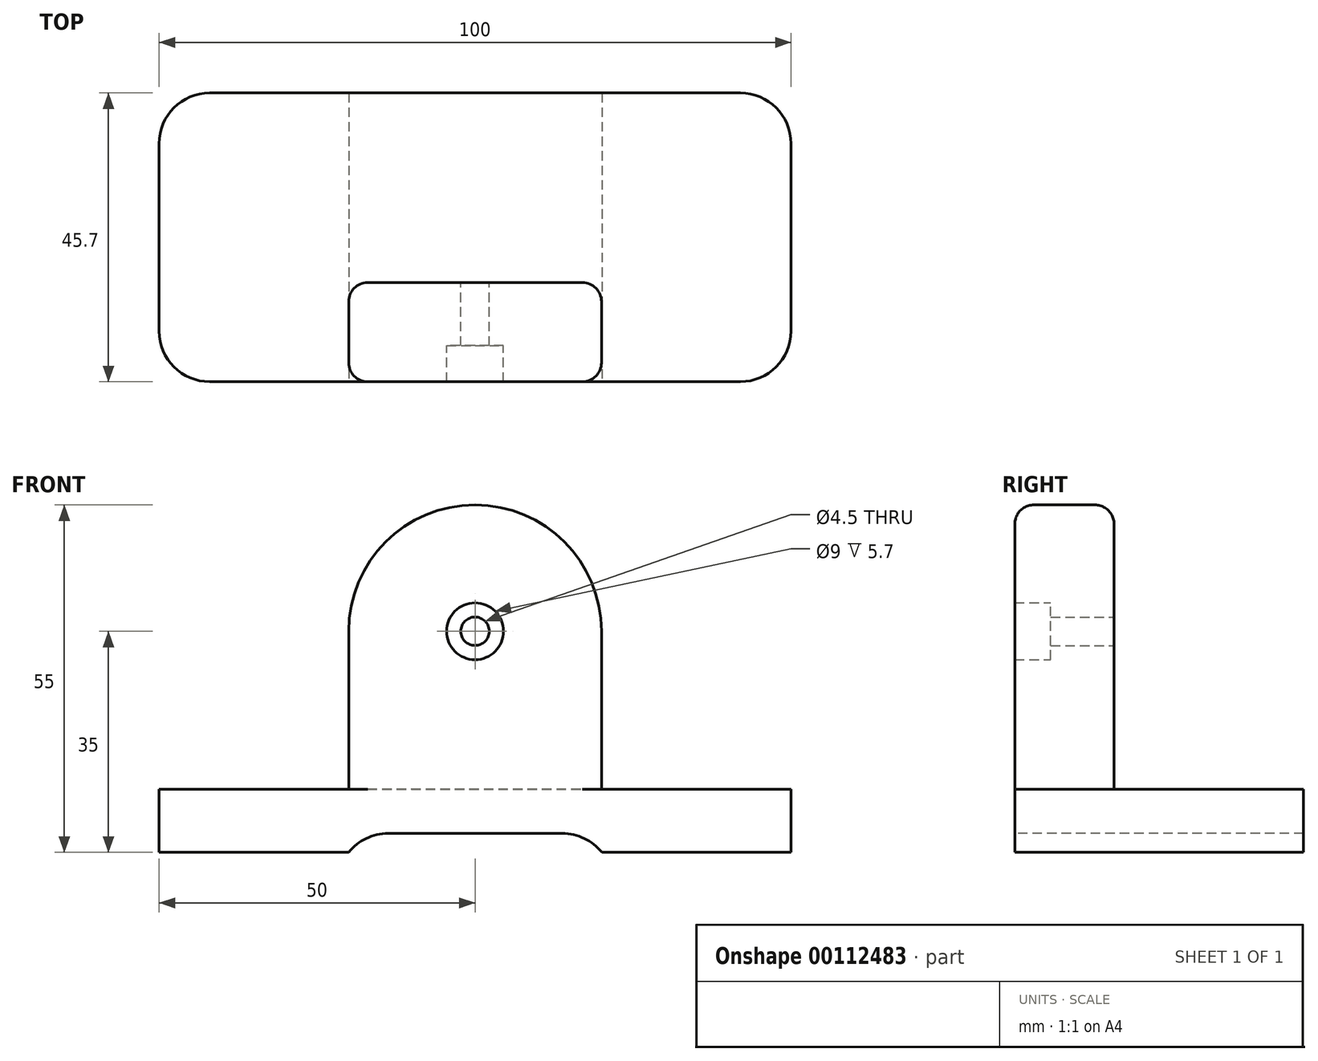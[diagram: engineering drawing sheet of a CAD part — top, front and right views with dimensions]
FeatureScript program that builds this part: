
annotation { "Feature Type Name" : "Feature", "Feature Type Description" : "" }
export const myFeature = defineFeature(function(context is Context, id is Id, definition is map)
    precondition{}
    {
        {
            var Q0;
            Q0=qCreatedBy(makeId("Top.planeOp"),FACE);
            var sketch = newSketch(context, id + "F0", { "sketchPlane" : qUnion([Q0])});
            skLineSegment(sketch, "E0.bottom", {"start": v(0, 0) * mm, "end": v(-100, 0) * mm});
            skLineSegment(sketch, "E0.top", {"start": v(0, 40) * mm, "end": v(-100, 40) * mm});
            skLineSegment(sketch, "E0.left", {"start": v(0, 0) * mm, "end": v(0, 40) * mm});
            skLineSegment(sketch, "E0.right", {"start": v(-100, 0) * mm, "end": v(-100, 40) * mm});
            skSolve(sketch);
        }
        {
            var Q0;
            Q0 = qSketchRegion(id + "F0", true);
            extrude(context, id + "F1", {"entities" : qUnion([Q0]), "depth" : 10 * mm});
        }
        {
            var Q0;
            Q0=makeQuery(id+"F1.opExtrude","SWEPT_FACE",FACE,{"disambiguationData":[OSD([sQuery(id+"F0.wireOp",EDGE,"E0.bottom")])]});
            var sketch = newSketch(context, id + "F2", { "sketchPlane" : qUnion([Q0])});
            skLineSegment(sketch, "E1", {"start": v(-70, 35) * mm, "end": v(-70, 0) * mm});
            skLineSegment(sketch, "E2", {"start": v(-70, 0) * mm, "end": v(-30, 0) * mm});
            skLineSegment(sketch, "E3", {"start": v(-30, 0) * mm, "end": v(-30, 35) * mm});
            skArc(sketch, "E4", {"start": v(-70, 35) * mm, "mid": v(-50, 55) * mm, "end": v(-30, 35) * mm});
            skSolve(sketch);
        }
        {
            var Q0;
            Q0 = qSketchRegion(id + "F2", true);
            extrude(context, id + "F3", {"entities" : qUnion([Q0]), "operationType" : NewBodyOperationType.ADD, "oppositeDirection" : true, "depth" : 10 * mm});
        }
        {
            var Q0;
            Q0=makeQuery(id+"F3.boolean.opBoolean","MERGE",FACE,{"derivedFrom":[makeQuery(id+"F1.opExtrude","SWEPT_FACE",FACE,{"disambiguationData":[OSD([sQuery(id+"F0.wireOp",EDGE,"E0.bottom")])]}),makeQuery(id+"F3.opExtrude","CAP_FACE",FACE,{"disambiguationData":[OSD([sQuery(id+"F2.wireOp",EDGE,"E1"),sQuery(id+"F2.wireOp",EDGE,"E2"),sQuery(id+"F2.wireOp",EDGE,"E3"),sQuery(id+"F2.wireOp",EDGE,"E4")])],"isStart":true})]});
            var sketch = newSketch(context, id + "F4", { "sketchPlane" : qUnion([Q0])});
            skLineSegment(sketch, "E5.bottom", {"start": v(-29.94, 0) * mm, "end": v(-70, 0) * mm});
            skLineSegment(sketch, "E5.top", {"start": v(-29.94, 3) * mm, "end": v(-70, 3) * mm});
            skLineSegment(sketch, "E5.left", {"start": v(-29.94, 0) * mm, "end": v(-29.94, 3) * mm});
            skLineSegment(sketch, "E5.right", {"start": v(-70, 0) * mm, "end": v(-70, 3) * mm});
            skSolve(sketch);
        }
        {
            var Q0;
            Q0 = qSketchRegion(id + "F4", true);
            extrude(context, id + "F5", {"entities" : qUnion([Q0]), "operationType" : NewBodyOperationType.REMOVE, "endBound" : BoundingType.THROUGH_ALL, "oppositeDirection" : true, "depth" : 25 * mm});
        }
        {
            var Q0;
            Q0=makeQuery(id+"F3.opExtrude","CAP_FACE",FACE,{"disambiguationData":[OSD([sQuery(id+"F2.wireOp",EDGE,"E1"),sQuery(id+"F2.wireOp",EDGE,"E2"),sQuery(id+"F2.wireOp",EDGE,"E3"),sQuery(id+"F2.wireOp",EDGE,"E4")])],"isStart":false});
            var sketch = newSketch(context, id + "F6", { "sketchPlane" : qUnion([Q0])});
            skCircle(sketch, "E6", {"center": v(50, 35) * mm, "radius": 2.25 * mm});
            skSolve(sketch);
        }
        {
            var Q0;
            Q0 = qSketchRegion(id + "F6", true);
            extrude(context, id + "F7", {"entities" : qUnion([Q0]), "operationType" : NewBodyOperationType.REMOVE, "endBound" : BoundingType.THROUGH_ALL, "oppositeDirection" : true, "depth" : 25 * mm});
        }
        {
            var Q0;
            Q0=makeQuery(id+"F3.boolean.opBoolean","MERGE",FACE,{"derivedFrom":[makeQuery(id+"F1.opExtrude","SWEPT_FACE",FACE,{"disambiguationData":[OSD([sQuery(id+"F0.wireOp",EDGE,"E0.bottom")])]}),makeQuery(id+"F3.opExtrude","CAP_FACE",FACE,{"disambiguationData":[OSD([sQuery(id+"F2.wireOp",EDGE,"E1"),sQuery(id+"F2.wireOp",EDGE,"E2"),sQuery(id+"F2.wireOp",EDGE,"E3"),sQuery(id+"F2.wireOp",EDGE,"E4")])],"isStart":true})]});
            var sketch = newSketch(context, id + "F8", { "sketchPlane" : qUnion([Q0])});
            skCircle(sketch, "E7", {"center": v(-50, 35) * mm, "radius": 4.5 * mm});
            skSolve(sketch);
        }
        {
            var Q0;
            Q0=sQuery(id+"F8.wireOp",EDGE,"E7");
            extrude(context, id + "F9", {"bodyType" : ToolBodyType.SURFACE, "surfaceEntities" : qUnion([Q0]), "depth" : 5.7 * mm});
        }
        {
            var Q0;
            Q0=makeQuery(id+"F8.imprint","IMPRINT",FACE,{"disambiguationData":[TD([[makeQuery(id+"F8.imprint","IMPRINT",EDGE,{"derivedFrom":sQuery(id+"F8.wireOp",EDGE,"E7")}),-1.0]])]});
            extrude(context, id + "F10", {"entities" : qUnion([Q0]), "operationType" : NewBodyOperationType.ADD, "depth" : 5.7 * mm});
        }
        {
            var Q0;
            {var subQ0=sQuery(id+"F4.wireOp",EDGE,"E5.left");var subQ1=sQuery(id+"F4.wireOp",EDGE,"E5.top");Q0=makeQuery(id+"F10.boolean.opBoolean","MERGE",EDGE,{"derivedFrom":[makeQuery(id+"F5.boolean.opBoolean","COPY",EDGE,{"derivedFrom":makeQuery(id+"F5.opExtrude","SWEPT_EDGE",EDGE,{"disambiguationData":[OSD([subQ1,subQ0])]})}),makeQuery(id+"F10.opExtrude","SWEPT_EDGE",EDGE,{"disambiguationData":[OSD([subQ1,subQ0])]})]});}
            var Q1;
            {var subQ0=sQuery(id+"F4.wireOp",EDGE,"E5.right");var subQ1=sQuery(id+"F4.wireOp",EDGE,"E5.top");Q1=makeQuery(id+"F10.boolean.opBoolean","MERGE",EDGE,{"derivedFrom":[makeQuery(id+"F5.boolean.opBoolean","COPY",EDGE,{"derivedFrom":makeQuery(id+"F5.opExtrude","SWEPT_EDGE",EDGE,{"disambiguationData":[OSD([subQ1,subQ0])]})}),makeQuery(id+"F10.opExtrude","SWEPT_EDGE",EDGE,{"disambiguationData":[OSD([subQ1,subQ0])]})]});}
            var Q2;
            Q2=makeQuery(id+"F1.opExtrude","SWEPT_EDGE",EDGE,{"disambiguationData":[OSD([sQuery(id+"F0.wireOp",EDGE,"E0.top"),sQuery(id+"F0.wireOp",EDGE,"E0.left")])]});
            var Q3;
            Q3=makeQuery(id+"F10.opExtrude","CAP_EDGE",EDGE,{"disambiguationData":[OSD([sQuery(id+"F0.wireOp",EDGE,"E0.bottom"),sQuery(id+"F0.wireOp",EDGE,"E0.left")])],"isStart":false});
            var Q4;
            Q4=makeQuery(id+"F10.opExtrude","CAP_EDGE",EDGE,{"disambiguationData":[OSD([sQuery(id+"F0.wireOp",EDGE,"E0.bottom"),sQuery(id+"F0.wireOp",EDGE,"E0.right")])],"isStart":false});
            var Q5;
            Q5=makeQuery(id+"F1.opExtrude","SWEPT_EDGE",EDGE,{"disambiguationData":[OSD([sQuery(id+"F0.wireOp",EDGE,"E0.top"),sQuery(id+"F0.wireOp",EDGE,"E0.right")])]});
            fillet(context, id + "F11", {"entities" : qUnion([Q0, Q1, Q2, Q3, Q4, Q5]), "radius" : 8 * mm, "tangentPropagation" : true, "allowEdgeOverflow" : false});
        }
        {
            var Q0;
            Q0=makeQuery(id+"F10.opExtrude","CAP_EDGE",EDGE,{"disambiguationData":[OSD([sQuery(id+"F2.wireOp",EDGE,"E3")])],"isStart":false});
            var Q1;
            Q1=makeQuery(id+"F10.opExtrude","CAP_EDGE",EDGE,{"disambiguationData":[OSD([sQuery(id+"F2.wireOp",EDGE,"E4")])],"isStart":false});
            var Q2;
            Q2=makeQuery(id+"F3.opExtrude","CAP_EDGE",EDGE,{"disambiguationData":[OSD([sQuery(id+"F2.wireOp",EDGE,"E4")])],"isStart":false});
            fillet(context, id + "F12", {"entities" : qUnion([Q0, Q1, Q2]), "radius" : 3 * mm, "tangentPropagation" : true, "allowEdgeOverflow" : false});
        }
    });
